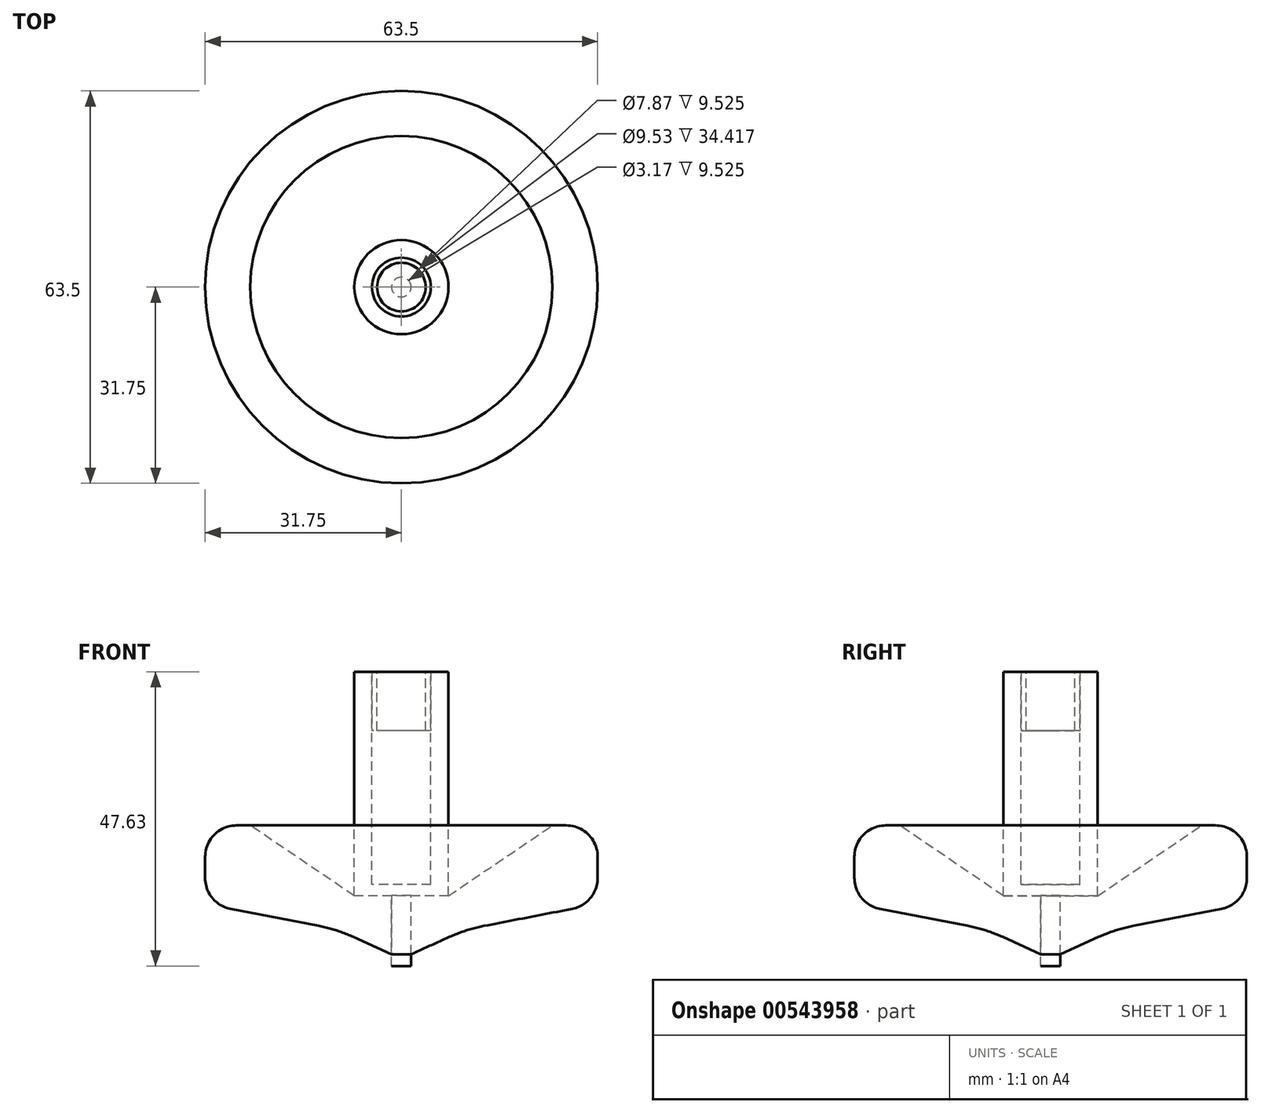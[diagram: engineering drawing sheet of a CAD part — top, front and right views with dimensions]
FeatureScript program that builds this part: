
annotation { "Feature Type Name" : "Feature", "Feature Type Description" : "" }
export const myFeature = defineFeature(function(context is Context, id is Id, definition is map)
    precondition{}
    {
        {
            var Q0;
            Q0=qCreatedBy(makeId("Front.planeOp"),FACE);
            var sketch = newSketch(context, id + "F0", { "sketchPlane" : qUnion([Q0])});
            skLineSegment(sketch, "E0", {"start": v(31.75, 8.13) * mm, "end": v(31.75, 20.83) * mm});
            skLineSegment(sketch, "E1", {"start": v(31.75, 20.83) * mm, "end": v(24.44, 20.83) * mm});
            skLineSegment(sketch, "E2", {"start": v(24.44, 20.83) * mm, "end": v(7.62, 9.44) * mm});
            skLineSegment(sketch, "E3", {"start": v(7.62, 9.44) * mm, "end": v(7.62, 45.72) * mm});
            skLineSegment(sketch, "E4", {"start": v(7.62, 45.72) * mm, "end": v(0, 45.72) * mm});
            skLineSegment(sketch, "E5", {"start": v(0, 45.72) * mm, "end": v(0, 0) * mm});
            skLineSegment(sketch, "E6", {"start": v(10.5, 4.02) * mm, "end": v(31.75, 8.13) * mm});
            skLineSegment(sketch, "E7", {"start": v(0, 0) * mm, "end": v(1.59, 0) * mm});
            skLineSegment(sketch, "E8", {"start": v(1.59, 0) * mm, "end": v(10.5, 4.02) * mm});
            skSolve(sketch);
        }
        {
            var Q0;
            Q0=qSketchRegion(id+"F0",true);
            var Q1;
            Q1=sQuery(id+"F0.wireOp",EDGE,"E5");
            revolve(context, id + "F1", {"entities" : qUnion([Q0]), "axis" : qUnion([Q1]), "revolveType" : RevolveType.FULL});
        }
        {
            var Q0;
            Q0=makeQuery(id+"F1.opRevolve","SWEPT_FACE",FACE,{"disambiguationData":[OSD([sQuery(id+"F0.wireOp",EDGE,"E0")])]});
            fillet(context, id + "F2", {"entities" : qUnion([Q0]), "radius" : 5.08 * mm, "tangentPropagation" : true, "allowEdgeOverflow" : false});
        }
        {
            var Q0;
            Q0=makeQuery(id+"F1.opRevolve","SWEPT_EDGE",EDGE,{"disambiguationData":[OSD([sQuery(id+"F0.wireOp",EDGE,"E6"),sQuery(id+"F0.wireOp",EDGE,"E8")])]});
            fillet(context, id + "F3", {"entities" : qUnion([Q0]), "radius" : 25.4 * mm, "tangentPropagation" : true, "allowEdgeOverflow" : false});
        }
        {
            var Q0;
            Q0=makeQuery(id+"F1.opRevolve","SWEPT_FACE",FACE,{"disambiguationData":[OSD([sQuery(id+"F0.wireOp",EDGE,"E4")])]});
            var sketch = newSketch(context, id + "F4", { "sketchPlane" : qUnion([Q0])});
            skCircle(sketch, "E9", {"center": v(0, 0) * mm, "radius": 4.76 * mm});
            skSolve(sketch);
        }
        {
            var Q0;
            Q0=qSketchRegion(id+"F4",true);
            extrude(context, id + "F5", {"entities" : qUnion([Q0]), "operationType" : NewBodyOperationType.REMOVE, "oppositeDirection" : true, "depth" : 9.52 * mm});
        }
        {
            var Q0;
            Q0=qCreatedBy(makeId("Top.planeOp"),FACE);
            var sketch = newSketch(context, id + "F6", { "sketchPlane" : qUnion([Q0])});
            skCircle(sketch, "E10", {"center": v(0, 0) * mm, "radius": 1.59 * mm});
            skSolve(sketch);
        }
        {
            var Q0;
            Q0=qSketchRegion(id+"F6",true);
            extrude(context, id + "F7", {"entities" : qUnion([Q0]), "operationType" : NewBodyOperationType.REMOVE, "depth" : 9.52 * mm, "offsetDistance" : 25.4 * mm});
        }
        {
            var Q0;
            Q0=makeQuery(id+"F5.boolean.opBoolean","COPY",FACE,{"derivedFrom":makeQuery(id+"F5.opExtrude","CAP_FACE",FACE,{"disambiguationData":[OSD([sQuery(id+"F4.wireOp",EDGE,"E9")])],"isStart":false})});
            extrude(context, id + "F8", {"entities" : qUnion([Q0]), "depth" : 9.52 * mm, "offsetDistance" : 25.4 * mm});
        }
        {
            var Q0;
            Q0=makeQuery(id+"F5.boolean.opBoolean","COPY",FACE,{"derivedFrom":makeQuery(id+"F5.opExtrude","CAP_FACE",FACE,{"disambiguationData":[OSD([sQuery(id+"F4.wireOp",EDGE,"E9")])],"isStart":false})});
            extrude(context, id + "F9", {"entities" : qUnion([Q0]), "operationType" : NewBodyOperationType.REMOVE, "oppositeDirection" : true, "depth" : 24.9 * mm});
        }
        {
            var Q0;
            Q0=makeQuery(id+"F8.opExtrude","CAP_FACE",FACE,{"disambiguationData":[OSD([sQuery(id+"F4.wireOp",EDGE,"E9")])],"isStart":false});
            var sketch = newSketch(context, id + "F10", { "sketchPlane" : qUnion([Q0])});
            skCircle(sketch, "E11", {"center": v(0, 0) * mm, "radius": 3.94 * mm});
            skSolve(sketch);
        }
        {
            var Q0;
            Q0=makeQuery(id+"F10.imprint","IMPRINT",FACE,{"disambiguationData":[TD([[makeQuery(id+"F10.imprint","IMPRINT",EDGE,{"derivedFrom":sQuery(id+"F10.wireOp",EDGE,"E11")}),1.0]])]});
            var Q1;
            Q1=sQuery(id+"F10.wireOp",EDGE,"E11");
            extrude(context, id + "F11", {"entities" : qUnion([Q0]), "operationType" : NewBodyOperationType.REMOVE, "surfaceEntities" : qUnion([Q1]), "oppositeDirection" : true, "depth" : 9.52 * mm, "offsetDistance" : 25.4 * mm});
        }
        {
            var Q0;
            Q0=makeQuery(id+"F7.boolean.opBoolean","COPY",FACE,{"derivedFrom":makeQuery(id+"F7.opExtrude","CAP_FACE",FACE,{"disambiguationData":[OSD([sQuery(id+"F6.wireOp",EDGE,"E10")])],"isStart":false})});
            extrude(context, id + "F12", {"entities" : qUnion([Q0]), "depth" : 11.43 * mm, "offsetDistance" : 25.4 * mm});
        }
    });
